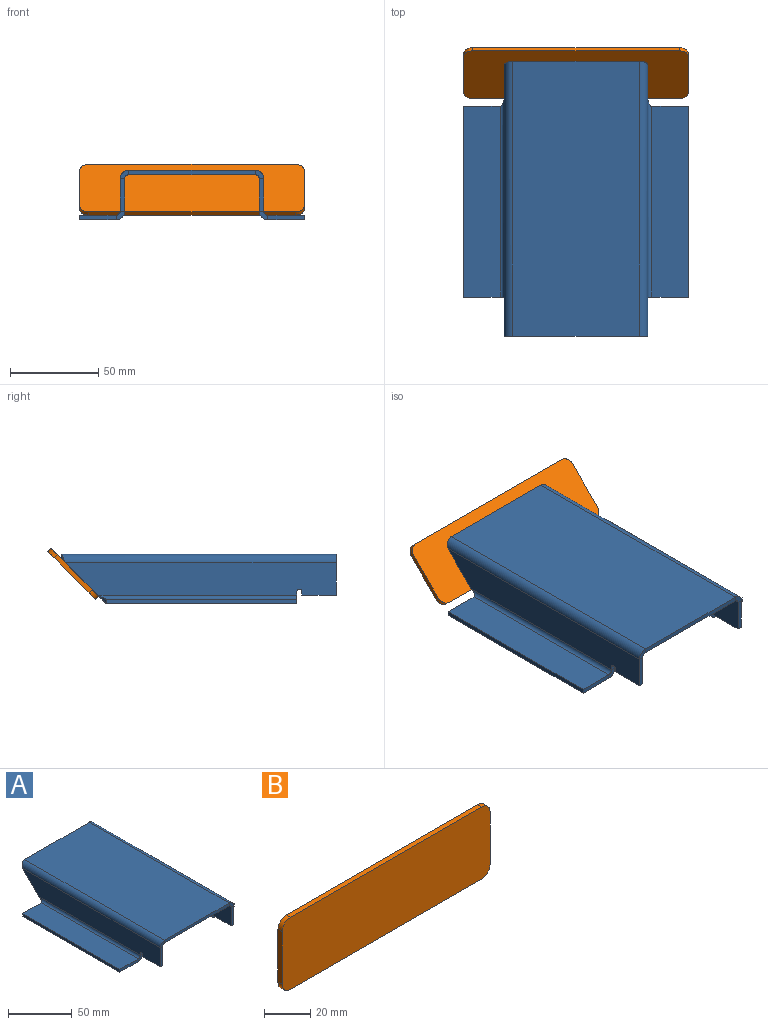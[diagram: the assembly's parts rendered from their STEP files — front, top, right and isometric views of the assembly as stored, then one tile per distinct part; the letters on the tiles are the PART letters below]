
ASSEMBLY  parts=2 mates=1
PART A: 46 faces, bbox 127x155.5x27.9 mm
  f0: plane 71.63x2.54mm, normal (0,-1,0), area 181.9mm2, adj f2,f3,f22,f42
  f1: plane 71.63x2.54mm, normal (0,1,0), area 181.9mm2, adj f2,f3,f21,f43
  f2: plane 155.47x71.63mm, normal (0,0,-1), area 11135.9mm2, adj f0,f1,f24,f45
  f3: plane 155.47x71.63mm, normal (0,0,1), area 11135.9mm2, adj f0,f1,f23,f44
  f4: plane 18.29x2.54mm, normal (0,-1,0), area 46.5mm2, adj f6,f7,f8,f22
  f5: plane 18.29x18.29mm, normal (0,0.71,-0.71), area 65.7mm2, adj f7,f8,f17,f21
  f6: plane 19.53x2.54mm, normal (0,0,-1), area 49.6mm2, adj f4,f7,f8,f10
  f7: plane 153.18x18.29mm, normal (-1,0,0), area 2625.7mm2, adj f4,f5,f6,f9,f10,f11,f19,f24
  f8: plane 153.18x18.29mm, normal (1,0,0), area 2625.7mm2, adj f4,f5,f6,f9,f10,f11,f20,f23
  f9: cylinder r=1.35mm len=2.7mm, axis (1,0,0), area 10.8mm2, adj f7,f8,f10,f11
  f10: plane 2.54x2.08mm, normal (0,1,0), area 5.3mm2, adj f6,f7,f8,f9
  f11: plane 2.54x2.08mm, normal (0,-1,0), area 5.3mm2, adj f7,f8,f9,f18
  f12: plane 20.57x2.54mm, normal (0,1,0), area 52.3mm2, adj f13,f15,f16,f17
  f13: plane 107.84x2.54mm, normal (1,0,0), area 273.9mm2, adj f12,f14,f15,f16
  f14: plane 20.57x2.54mm, normal (0,-1,0), area 52.3mm2, adj f13,f15,f16,f18
  f15: plane 107.84x20.57mm, normal (0,0,-1), area 2218.8mm2, adj f12,f13,f14,f19
  f16: plane 107.84x20.57mm, normal (0,0,1), area 2218.8mm2, adj f12,f13,f14,f20
  f17: bspline ~4.83x4.83mm, area 19.5mm2, adj f5,f12,f19,f20
  f18: plane 4.83x4.83mm, normal (0,-1,0), area 14.2mm2, adj f11,f14,f19,f20
  f19: cylinder r=4.83mm len=112.67mm, axis (0,1,0), area 830.8mm2, adj f7,f15,f17,f18
  f20: cylinder r=2.29mm len=112.67mm, axis (0,1,0), area 393.5mm2, adj f8,f16,f17,f18
  f21: bspline ~4.83x4.83mm, area 15.6mm2, adj f1,f5,f23,f24
  f22: plane 4.83x4.83mm, normal (0,-1,0), area 14.2mm2, adj f0,f4,f23,f24
  f23: cylinder r=4.83mm len=155.47mm, axis (0,1,0), area 1172.2mm2, adj f3,f8,f21,f22
  f24: cylinder r=2.29mm len=155.47mm, axis (0,1,0), area 555.3mm2, adj f2,f7,f21,f22
  f25: plane 19.53x2.54mm, normal (0,0,-1), area 49.6mm2, adj f26,f27,f29,f32
  f26: plane 153.18x18.29mm, normal (1,0,0), area 2625.7mm2, adj f25,f28,f29,f30,f31,f32,f40,f45
  f27: plane 153.18x18.29mm, normal (-1,0,0), area 2625.7mm2, adj f25,f28,f29,f30,f31,f32,f41,f44
  f28: plane 18.29x18.29mm, normal (0,0.71,-0.71), area 65.7mm2, adj f26,f27,f39,f43
  f29: plane 18.29x2.54mm, normal (0,-1,0), area 46.5mm2, adj f25,f26,f27,f42
  f30: cylinder r=1.35mm len=2.7mm, axis (-1,0,0), area 10.8mm2, adj f26,f27,f31,f32
  f31: plane 2.54x2.08mm, normal (0,-1,0), area 5.3mm2, adj f26,f27,f30,f38
  f32: plane 2.54x2.08mm, normal (0,1,0), area 5.3mm2, adj f25,f26,f27,f30
  f33: plane 107.84x2.54mm, normal (-1,0,0), area 273.9mm2, adj f34,f35,f36,f37
  f34: plane 20.57x2.54mm, normal (0,1,0), area 52.3mm2, adj f33,f36,f37,f39
  f35: plane 20.57x2.54mm, normal (0,-1,0), area 52.3mm2, adj f33,f36,f37,f38
  f36: plane 107.84x20.57mm, normal (0,0,-1), area 2218.8mm2, adj f33,f34,f35,f40
  f37: plane 107.84x20.57mm, normal (0,0,1), area 2218.8mm2, adj f33,f34,f35,f41
  f38: plane 4.83x4.83mm, normal (0,-1,0), area 14.2mm2, adj f31,f35,f40,f41
  f39: bspline ~4.83x4.83mm, area 19.4mm2, adj f28,f34,f40,f41
  f40: cylinder r=4.83mm len=112.67mm, axis (0,-1,0), area 830.8mm2, adj f26,f36,f38,f39
  f41: cylinder r=2.29mm len=112.67mm, axis (0,-1,0), area 393.6mm2, adj f27,f37,f38,f39
  f42: plane 4.83x4.83mm, normal (0,-1,0), area 14.2mm2, adj f0,f29,f44,f45
  f43: bspline ~4.83x4.83mm, area 15.6mm2, adj f1,f28,f44,f45
  f44: cylinder r=4.83mm len=155.47mm, axis (0,-1,0), area 1172.3mm2, adj f3,f27,f42,f43
  f45: cylinder r=2.29mm len=155.47mm, axis (0,-1,0), area 555.3mm2, adj f2,f26,f42,f43
PART B: 10 faces, bbox 127x2.5x38.1 mm
  f0: plane 27.94x2.54mm, normal (-1,0,0), area 71mm2, adj f4,f5,f6,f9
  f1: plane 116.84x2.54mm, normal (0,0,1), area 296.8mm2, adj f4,f5,f6,f7
  f2: plane 27.94x2.54mm, normal (1,0,0), area 71mm2, adj f4,f5,f7,f8
  f3: plane 116.84x2.54mm, normal (0,0,-1), area 296.8mm2, adj f4,f5,f8,f9
  f4: plane 127x38.1mm, normal (0,1,0), area 4816.5mm2, adj f0,f1,f2,f3,f6,f7,f8,f9
  f5: plane 127x38.1mm, normal (0,-1,0), area 4816.5mm2, adj f0,f1,f2,f3,f6,f7,f8,f9
  f6: cylinder r=5.08mm len=5.08mm, axis (0,1,0), area 20.3mm2, adj f0,f1,f4,f5
  f7: cylinder r=5.08mm len=5.08mm, axis (0,-1,0), area 20.3mm2, adj f1,f2,f4,f5
  f8: cylinder r=5.08mm len=5.08mm, axis (0,1,0), area 20.3mm2, adj f2,f3,f4,f5
  f9: cylinder r=5.08mm len=5.08mm, axis (0,-1,0), area 20.3mm2, adj f0,f3,f4,f5
PLACE A t=(-32.86,-31.91,4.01)mm
PLACE B rot(axis=(-1,0,0),45deg) t=(-32.86,44.87,-5.35)mm
MATE fastened B.f5 <-> A.f5  axis (0,-0.71,0.71) through (30.64,43.07,-3.56)mm
